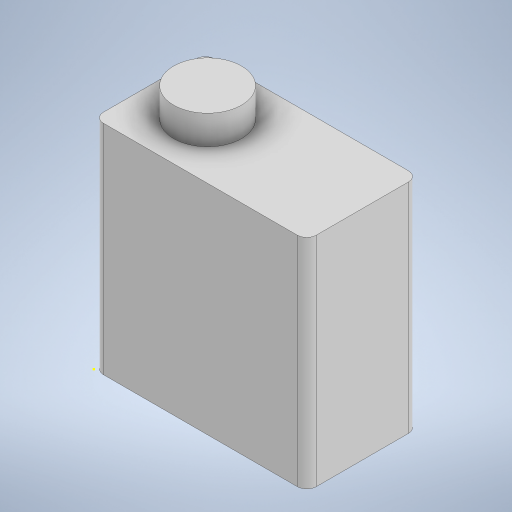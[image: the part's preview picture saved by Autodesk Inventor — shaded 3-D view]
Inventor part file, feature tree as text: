
AUTODESK INVENTOR PART (.ipt)
format: ipt  version: 2023 (Build 270158000, 158)  size: 248,320 bytes
history: native  units: mm
features: sketch x3, extrude x2, fillet x1
ambient origin geometry x8: Origin, YZ Plane, XZ Plane, XY Plane, X Axis, Y Axis, Z Axis, Center Point
bodies: Solid1 (feature_tree)
feature tree (6):
  extrude  "Extrusion1"  Depth=11.5mm
  fillet  "Fillet1"  Radius=22.5mm
  sketch  "Sketch2"  dims[d4=1.0mm d5=7.0mm]
  extrude  "Extrusion2"  Depth=1.0mm
  sketch  "Sketch1"  dims[d0=22.0mm d1=11.5mm d2=22.5mm d3=0.0mm]
  sketch  "Sketch3"  dims[d6=16.0mm d7=5.75mm d8=3.0mm d9=0.0mm]
